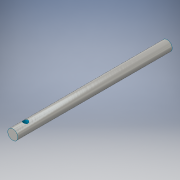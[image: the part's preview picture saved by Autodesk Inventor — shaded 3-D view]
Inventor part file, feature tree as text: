
AUTODESK INVENTOR PART (.ipt)
format: ipt  version: 2016 (Build 200138000, 138)  size: 101,376 bytes
history: native  units: in
note: dims shown in document units (in); Inventor stores cm internally (conversion verified against a paired STEP export)
features: extrude x2, sketch x2
ambient origin geometry x8: Origin, YZ Plane, XZ Plane, XY Plane, X Axis, Y Axis, Z Axis, Center Point
bodies: Solid1 (feature_tree)
feature tree (4):
  extrude  "Extrusion1"  Depth=3.8189in TaperAngle=0.0deg
  extrude  "Extrusion2"  Depth=0.1181in
  sketch  "Sketch1"  dims[d0=0.25in d1=3.8189in d2=0.0in]
  sketch  "Sketch2"  dims[d3=0.315in d4=0.1181in d5=0.252in d6=0.0in]
